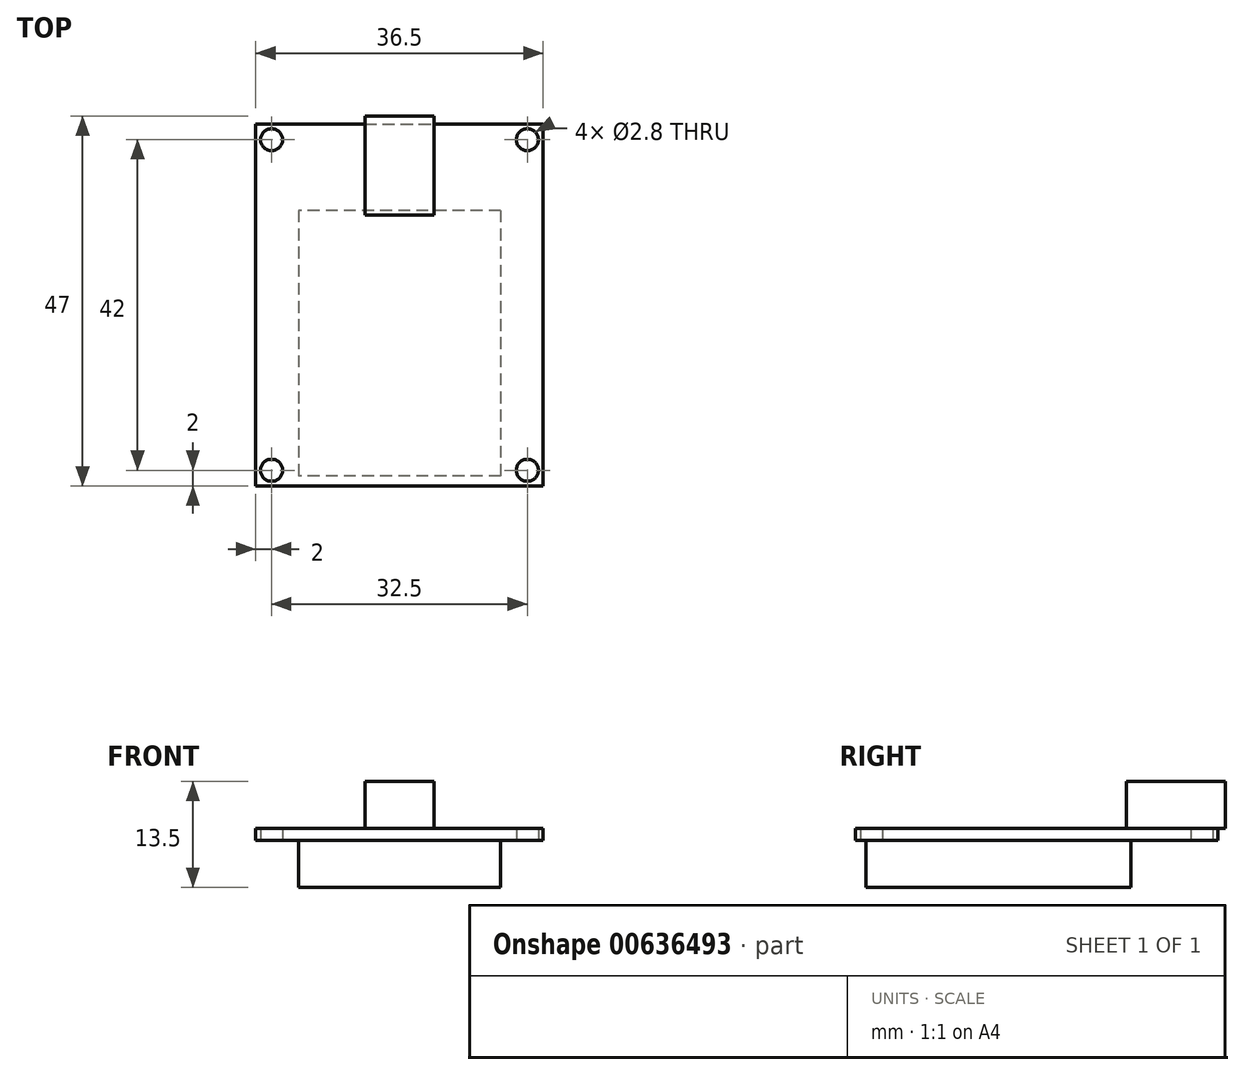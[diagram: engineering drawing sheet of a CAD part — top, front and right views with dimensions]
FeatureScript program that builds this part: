
annotation { "Feature Type Name" : "Feature", "Feature Type Description" : "" }
export const myFeature = defineFeature(function(context is Context, id is Id, definition is map)
    precondition{}
    {
        {
            var Q0;
            Q0=qCreatedBy(makeId("Top.planeOp"),FACE);
            var sketch = newSketch(context, id + "F0", { "sketchPlane" : qUnion([Q0])});
            skLineSegment(sketch, "E0.bottom", {"start": v(-36.5, 46) * mm, "end": v(0, 46) * mm});
            skLineSegment(sketch, "E0.top", {"start": v(-36.5, 0) * mm, "end": v(0, 0) * mm});
            skLineSegment(sketch, "E0.left", {"start": v(-36.5, 46) * mm, "end": v(-36.5, 0) * mm});
            skLineSegment(sketch, "E0.right", {"start": v(0, 46) * mm, "end": v(0, 0) * mm});
            skLineSegment(sketch, "E1", {"start": v(-34.5, 46) * mm, "end": v(-34.5, 41.43) * mm, "construction": true});
            skLineSegment(sketch, "E2", {"start": v(-36.5, 44) * mm, "end": v(-29.28, 44) * mm, "construction": true});
            skCircle(sketch, "E3", {"center": v(-34.5, 44) * mm, "radius": 1.4 * mm});
            skCircle(sketch, "E4.1.0.0", {"center": v(-2, 44) * mm, "radius": 1.4 * mm});
            skLineSegment(sketch, "E4.direction1", {"start": v(-34.5, 44) * mm, "end": v(-2, 44) * mm, "construction": true});
            skLineSegment(sketch, "E5", {"start": v(-36.5, 23) * mm, "end": v(0, 23) * mm, "construction": true});
            skCircle(sketch, "E6.MirrorC", {"center": v(-34.5, 2) * mm, "radius": 1.4 * mm});
            skCircle(sketch, "E7.MirrorC", {"center": v(-2, 2) * mm, "radius": 1.4 * mm});
            skSolve(sketch);
        }
        {
            var Q0;
            Q0 = qSketchRegion(id + "F0", true);
            extrude(context, id + "F1", {"entities" : qUnion([Q0]), "depth" : 1.5 * mm, "offsetDistance" : 25 * mm});
        }
        {
            var Q0;
            Q0=makeQuery(id+"F1.opExtrude","CAP_FACE",FACE,{"disambiguationData":[OSD([sQuery(id+"F0.wireOp",EDGE,"E0.bottom"),sQuery(id+"F0.wireOp",EDGE,"E0.top"),sQuery(id+"F0.wireOp",EDGE,"E0.left"),sQuery(id+"F0.wireOp",EDGE,"E0.right"),sQuery(id+"F0.wireOp",EDGE,"E3"),sQuery(id+"F0.wireOp",EDGE,"E4.1.0.0"),sQuery(id+"F0.wireOp",EDGE,"E6.MirrorC"),sQuery(id+"F0.wireOp",EDGE,"E7.MirrorC")])],"isStart":false});
            var sketch = newSketch(context, id + "F2", { "sketchPlane" : qUnion([Q0])});
            skLineSegment(sketch, "E8", {"start": v(-18.25, 46) * mm, "end": v(-18.25, 49.64) * mm, "construction": true});
            skCircle(sketch, "E9", {"center": v(-18.25, 46) * mm, "radius": 1 * mm, "construction": true});
            skLineSegment(sketch, "E10", {"start": v(-18.25, 47) * mm, "end": v(-22.65, 47) * mm, "construction": true});
            skLineSegment(sketch, "E11.bottom", {"start": v(-22.65, 47) * mm, "end": v(-13.85, 47) * mm});
            skLineSegment(sketch, "E11.top", {"start": v(-22.65, 34.4) * mm, "end": v(-13.85, 34.4) * mm});
            skLineSegment(sketch, "E11.left", {"start": v(-22.65, 47) * mm, "end": v(-22.65, 34.4) * mm});
            skLineSegment(sketch, "E11.right", {"start": v(-13.85, 47) * mm, "end": v(-13.85, 34.4) * mm});
            skSolve(sketch);
        }
        {
            var Q0;
            Q0 = qSketchRegion(id + "F2", true);
            extrude(context, id + "F3", {"entities" : qUnion([Q0]), "operationType" : NewBodyOperationType.ADD, "depth" : 6 * mm, "offsetDistance" : 25 * mm});
        }
        {
            var Q0;
            Q0=makeQuery(id+"F1.opExtrude","CAP_FACE",FACE,{"disambiguationData":[OSD([sQuery(id+"F0.wireOp",EDGE,"E0.bottom"),sQuery(id+"F0.wireOp",EDGE,"E0.top"),sQuery(id+"F0.wireOp",EDGE,"E0.left"),sQuery(id+"F0.wireOp",EDGE,"E0.right"),sQuery(id+"F0.wireOp",EDGE,"E3"),sQuery(id+"F0.wireOp",EDGE,"E4.1.0.0"),sQuery(id+"F0.wireOp",EDGE,"E6.MirrorC"),sQuery(id+"F0.wireOp",EDGE,"E7.MirrorC")])],"isStart":true});
            var sketch = newSketch(context, id + "F4", { "sketchPlane" : qUnion([Q0])});
            skLineSegment(sketch, "E12", {"start": v(-18.25, 0) * mm, "end": v(-18.25, -46) * mm, "construction": true});
            skLineSegment(sketch, "E13", {"start": v(-18.25, -35) * mm, "end": v(-5.4, -35) * mm, "construction": true});
            skLineSegment(sketch, "E14.bottom", {"start": v(-5.4, -35) * mm, "end": v(-31.1, -35) * mm});
            skLineSegment(sketch, "E14.top", {"start": v(-5.4, -1.3) * mm, "end": v(-31.1, -1.3) * mm});
            skLineSegment(sketch, "E14.left", {"start": v(-5.4, -35) * mm, "end": v(-5.4, -1.3) * mm});
            skLineSegment(sketch, "E14.right", {"start": v(-31.1, -35) * mm, "end": v(-31.1, -1.3) * mm});
            skSolve(sketch);
        }
        {
            var Q0;
            Q0=makeQuery(id+"F4.imprint","IMPRINT",FACE,{"disambiguationData":[TD([[makeQuery(id+"F4.imprint","IMPRINT",EDGE,{"derivedFrom":sQuery(id+"F4.wireOp",EDGE,"E14.bottom")}),-1.0]])]});
            extrude(context, id + "F5", {"entities" : qUnion([Q0]), "operationType" : NewBodyOperationType.ADD, "depth" : 6 * mm, "offsetDistance" : 25 * mm});
        }
    });
